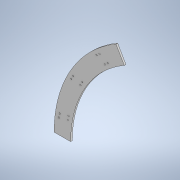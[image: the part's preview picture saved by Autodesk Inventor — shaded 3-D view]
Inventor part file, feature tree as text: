
AUTODESK INVENTOR PART (.ipt)
format: ipt  version: 2020.3 (Build 243373000, 373)  size: 140,800 bytes
history: native  units: mm
features: extrude x3, sketch x2, pattern_circular x1
ambient origin geometry x8: Origin, YZ Plane, XZ Plane, XY Plane, X Axis, Y Axis, Z Axis, Center Point
bodies: Solid1 (feature_tree)
feature tree (6):
  extrude  "Extrusion1"  Depth=40.0mm
  extrude  "Extrusion2"  Depth=10.0mm TaperAngle=0.0deg
  extrude  "Extrusion3"  Depth=10.0mm
  pattern_circular  "Circular Pattern1"  [2 undecoded]
  sketch  "Sketch1"  dims[d0=600.0mm d1=40.0mm]
  sketch  "Sketch3"  dims[d2=4.0mm d3=0.0mm d4=10.0mm d5=0.0mm d6=3.0mm d7=3.0mm d9=270.0mm d11=3.0mm d12=3.0mm d14=270.0mm d16=0.0mm d17=0.0mm d18=90.0mm d19=27.925268mm d21=20.071286mm d22=20.0mm d23=1.570796mm d24=1.919862mm d25=60.0deg]
note: 2 required parameter values undecoded (feature->parameter linkage not recoverable at this tier; creation-order binding heuristic only, values carry confidence <= 0.55)
